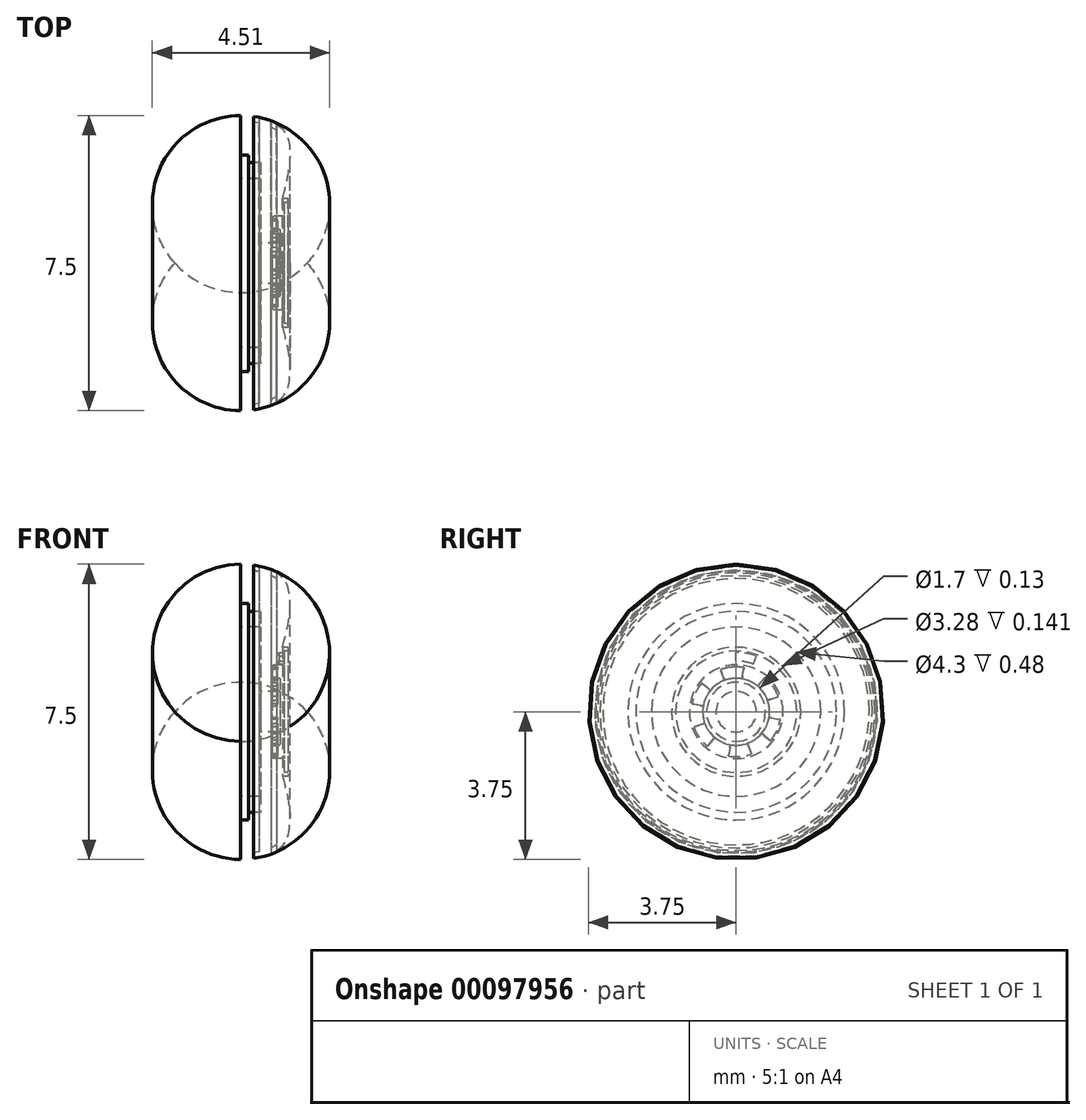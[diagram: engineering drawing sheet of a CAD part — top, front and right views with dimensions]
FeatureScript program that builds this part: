
annotation { "Feature Type Name" : "Feature", "Feature Type Description" : "" }
export const myFeature = defineFeature(function(context is Context, id is Id, definition is map)
    precondition{}
    {
        {
            var Q0;
            Q0=qCreatedBy(makeId("Front.planeOp"),FACE);
            var sketch = newSketch(context, id + "F0", { "sketchPlane" : qUnion([Q0])});
            skLineSegment(sketch, "E0.top", {"start": v(0.87, 0.85) * mm, "end": v(1, 0.85) * mm});
            skLineSegment(sketch, "E0.right", {"start": v(1, 0.51) * mm, "end": v(1, 0.85) * mm});
            skLineSegment(sketch, "E1", {"start": v(0.8, 0.93) * mm, "end": v(0.8, 1.1) * mm});
            skLineSegment(sketch, "E2", {"start": v(0.87, 1.19) * mm, "end": v(1.1, 1.19) * mm});
            skLineSegment(sketch, "E3", {"start": v(1.12, 1.64) * mm, "end": v(1.06, 1.64) * mm});
            skPoint(sketch, "E4.orphan", {"position": v(0, 1.19) * mm});
            skPoint(sketch, "E5.visualSharp", {"position": v(1.1, 1.19) * mm});
            skPoint(sketch, "E6.visualSharp", {"position": v(0.8, 1.19) * mm});
            skArc(sketch, "E6.filletArc", {"start": v(0.87, 1.19) * mm, "mid": v(0.81, 1.17) * mm, "end": v(0.8, 1.1) * mm});
            skArc(sketch, "E7.filletArc", {"start": v(0.8, 0.93) * mm, "mid": v(0.81, 0.87) * mm, "end": v(0.87, 0.85) * mm});
            skPoint(sketch, "E8.visualSharp", {"position": v(1.2, 1.64) * mm});
            skLineSegment(sketch, "E9", {"start": v(-0.76, 3.75) * mm, "end": v(0, 3.75) * mm, "construction": true});
            skLineSegment(sketch, "E10", {"start": v(1.25, 3.8) * mm, "end": v(1.25, 0.98) * mm, "construction": true});
            skLineSegment(sketch, "E11", {"start": v(0, 3.75) * mm, "end": v(1.72, 3.75) * mm, "construction": true});
            skLineSegment(sketch, "E12", {"start": v(1.25, 1.19) * mm, "end": v(1.27, 1.19) * mm});
            skLineSegment(sketch, "E13", {"start": v(1.1, 1.19) * mm, "end": v(1.1, 1.54) * mm});
            skPoint(sketch, "E14.orphan", {"position": v(0, 0.73) * mm});
            skLineSegment(sketch, "E15", {"start": v(0, 0.73) * mm, "end": v(0, 2.15) * mm, "construction": true});
            skLineSegment(sketch, "E16", {"start": v(0.5, 0.52) * mm, "end": v(1, 0.52) * mm});
            skLineSegment(sketch, "E17", {"start": v(0.57, 0) * mm, "end": v(0.57, -0.77) * mm, "construction": true});
            skLineSegment(sketch, "E18", {"start": v(1.1, 4.64) * mm, "end": v(1.1, 3.06) * mm, "construction": true});
            skLineSegment(sketch, "E19", {"start": v(0.97, 3.34) * mm, "end": v(1.1, 3.34) * mm, "construction": true});
            skFitSpline(sketch, "E20", {"points": [v(1.06, 1.64) * mm, v(1.25, 2.8) * mm, v(1.1, 3.34) * mm, v(0, 3.75) * mm], "startDerivative": vector(1.54, 5.67) * mm, "endDerivative": vector(-4.24, 0) * mm});
            skPoint(sketch, "E21", {"position": v(1.25, 2.38) * mm});
            skLineSegment(sketch, "E22", {"start": v(0.32, 3.93) * mm, "end": v(0.32, 3.59) * mm, "construction": true});
            skLineSegment(sketch, "E23", {"start": v(0.46, 3.93) * mm, "end": v(0.46, 3.56) * mm, "construction": true});
            skLineSegment(sketch, "E24", {"start": v(0.77, 3.93) * mm, "end": v(0.77, 3.46) * mm, "construction": true});
            skLineSegment(sketch, "E25", {"start": v(0.91, 3.95) * mm, "end": v(0.91, 3.38) * mm, "construction": true});
            skLineSegment(sketch, "E26", {"start": v(0.32, 3.59) * mm, "end": v(0.46, 3.56) * mm});
            skLineSegment(sketch, "E27", {"start": v(0.77, 3.46) * mm, "end": v(0.91, 3.38) * mm});
            skLineSegment(sketch, "E28", {"start": v(0.32, 3.73) * mm, "end": v(0.32, 3.59) * mm});
            skLineSegment(sketch, "E29", {"start": v(0.46, 3.56) * mm, "end": v(0.46, 3.7) * mm});
            skLineSegment(sketch, "E30", {"start": v(0.77, 3.46) * mm, "end": v(0.77, 3.6) * mm});
            skLineSegment(sketch, "E31", {"start": v(0.91, 3.38) * mm, "end": v(0.91, 3.52) * mm});
            skLineSegment(sketch, "E32", {"start": v(0, 0.52) * mm, "end": v(0, 2.15) * mm});
            skLineSegment(sketch, "E33", {"start": v(0.02, 0) * mm, "end": v(2.08, 0) * mm, "construction": true});
            skLineSegment(sketch, "E34", {"start": v(0, 0.51) * mm, "end": v(0, 2.15) * mm, "construction": true});
            skLineSegment(sketch, "E35", {"start": v(0, 0.52) * mm, "end": v(0, 0) * mm});
            skLineSegment(sketch, "E36", {"start": v(0, 0) * mm, "end": v(0.5, 0) * mm});
            skLineSegment(sketch, "E37", {"start": v(0.5, 0) * mm, "end": v(0.5, 0.52) * mm});
            skLineSegment(sketch, "E38", {"start": v(1.2, 1.54) * mm, "end": v(1.1, 1.54) * mm});
            skLineSegment(sketch, "E39", {"start": v(1.2, 1.64) * mm, "end": v(1.12, 1.64) * mm});
            skLineSegment(sketch, "E40", {"start": v(1.2, 1.64) * mm, "end": v(1.2, 1.54) * mm});
            skLineSegment(sketch, "E41", {"start": v(0, 2.75) * mm, "end": v(0.2, 2.75) * mm});
            skLineSegment(sketch, "E42", {"start": v(0.2, 2.75) * mm, "end": v(0.2, 2.55) * mm});
            skLineSegment(sketch, "E43", {"start": v(0.2, 2.55) * mm, "end": v(0.5, 2.55) * mm});
            skLineSegment(sketch, "E44", {"start": v(0.5, 2.55) * mm, "end": v(0.5, 2.15) * mm});
            skLineSegment(sketch, "E45", {"start": v(0.5, 2.15) * mm, "end": v(0.02, 2.15) * mm});
            skLineSegment(sketch, "E46.trimOffspring", {"start": v(0, 2.75) * mm, "end": v(0, 5.56) * mm, "construction": true});
            skLineSegment(sketch, "E47.trimOffspring", {"start": v(0, 2.75) * mm, "end": v(0, 5.2) * mm, "construction": true});
            skLineSegment(sketch, "E48.trimOffspring", {"start": v(0, 2.75) * mm, "end": v(0, 3.75) * mm});
            skLineSegment(sketch, "E49", {"start": v(0.02, 0) * mm, "end": v(0.02, 2.15) * mm});
            skSolve(sketch);
        }
        {
            var Q0;
            Q0=makeQuery(id+"F0.imprint","IMPRINT",FACE,{"disambiguationData":[TD([[makeQuery(id+"F0.imprint","IMPRINT",EDGE,{"derivedFrom":sQuery(id+"F0.wireOp",EDGE,"E0.top")}),-1.0]])]});
            var Q1;
            Q1=sQuery(id+"F0.wireOp",EDGE,"8bb111fc-4642-4fca-a44e-8b574824e9490.MirrorCS");
            var Q2;
            Q2=sQuery(id+"F0.wireOp",EDGE,"5d76dffb-9663-4801-85ba-127905f750e50.MirrorCS");
            var Q3;
            Q3=sQuery(id+"F0.wireOp",EDGE,"d13460d5-a523-4224-9297-77c6a2cba0c50.MirrorCS");
            var Q4;
            Q4=sQuery(id+"F0.wireOp",EDGE,"c0737af9-8dda-4185-ab45-cae04200aa6d0.MirrorCS");
            var Q5;
            Q5=sQuery(id+"F0.wireOp",EDGE,"E33");
            revolve(context, id + "F1", {"entities" : qUnion([Q0]), "surfaceEntities" : qUnion([Q1, Q2, Q3, Q4]), "axis" : qUnion([Q5]), "revolveType" : RevolveType.FULL});
        }
        {
            var Q0;
            Q0=qCreatedBy(makeId("Front.planeOp"),FACE);
            var sketch = newSketch(context, id + "F2", { "sketchPlane" : qUnion([Q0])});
            skLineSegment(sketch, "E50.bottom", {"start": v(0.97, 1.51) * mm, "end": v(1.17, 1.51) * mm});
            skLineSegment(sketch, "E50.top", {"start": v(0.97, 1.29) * mm, "end": v(1.17, 1.29) * mm});
            skLineSegment(sketch, "E50.left", {"start": v(0.97, 1.51) * mm, "end": v(0.97, 1.29) * mm});
            skLineSegment(sketch, "E50.right", {"start": v(1.17, 1.51) * mm, "end": v(1.17, 1.29) * mm});
            skLineSegment(sketch, "E51", {"start": v(0, 0) * mm, "end": v(2.72, 0) * mm, "construction": true});
            skSolve(sketch);
        }
        {
            var Q0;
            Q0=qSketchRegion(id+"F2",true);
            var Q1;
            Q1=sQuery(id+"F2.wireOp",EDGE,"E51");
            revolve(context, id + "F3", {"operationType" : NewBodyOperationType.REMOVE, "entities" : qUnion([Q0]), "axis" : qUnion([Q1]), "revolveType" : RevolveType.ONE_DIRECTION, "oppositeDirection" : true, "angle" : 20 * degree});
        }
        {
            var Q0;
            Q0=makeQuery(id+"F1.opRevolve","SWEPT_FACE",FACE,{"disambiguationData":[OSD([sQuery(id+"F0.wireOp",EDGE,"E1")])]});
            var sketch = newSketch(context, id + "F4", { "sketchPlane" : qUnion([Q0])});
            skLineSegment(sketch, "E52", {"start": v(-0.27, 0.74) * mm, "end": v(-0.39, 1.07) * mm});
            skArc(sketch, "E53", {"start": v(-0.39, 1.07) * mm, "mid": v(-0.1, 1.13) * mm, "end": v(0.2, 1.12) * mm});
            skLineSegment(sketch, "E54", {"start": v(0.14, 0.78) * mm, "end": v(0.2, 1.12) * mm});
            skArc(sketch, "E55", {"start": v(-0.27, 0.74) * mm, "mid": v(-0.07, 0.79) * mm, "end": v(0.14, 0.78) * mm});
            skLineSegment(sketch, "E56.1.0", {"start": v(-0.78, 0.14) * mm, "end": v(-1.12, 0.2) * mm});
            skArc(sketch, "E56.1.1", {"start": v(-1.12, 0.2) * mm, "mid": v(-1.03, 0.48) * mm, "end": v(-0.87, 0.73) * mm});
            skLineSegment(sketch, "E56.1.2", {"start": v(-0.6, 0.5) * mm, "end": v(-0.87, 0.73) * mm});
            skArc(sketch, "E56.1.3", {"start": v(-0.78, 0.14) * mm, "mid": v(-0.71, 0.33) * mm, "end": v(-0.6, 0.5) * mm});
            skLineSegment(sketch, "E56.2.0", {"start": v(-0.5, -0.6) * mm, "end": v(-0.73, -0.87) * mm});
            skArc(sketch, "E56.2.1", {"start": v(-0.73, -0.87) * mm, "mid": v(-0.93, -0.65) * mm, "end": v(-1.07, -0.39) * mm});
            skLineSegment(sketch, "E56.2.2", {"start": v(-0.74, -0.27) * mm, "end": v(-1.07, -0.39) * mm});
            skArc(sketch, "E56.2.3", {"start": v(-0.5, -0.6) * mm, "mid": v(-0.65, -0.45) * mm, "end": v(-0.74, -0.27) * mm});
            skLineSegment(sketch, "E57.1.3.0", {"start": v(0.27, -0.74) * mm, "end": v(0.39, -1.07) * mm});
            skArc(sketch, "E57.3.3.0", {"start": v(0.39, -1.07) * mm, "mid": v(0.1, -1.13) * mm, "end": v(-0.2, -1.12) * mm});
            skLineSegment(sketch, "E57.7.3.0", {"start": v(-0.14, -0.78) * mm, "end": v(-0.2, -1.12) * mm});
            skArc(sketch, "E57.10.3.0", {"start": v(0.27, -0.74) * mm, "mid": v(0.07, -0.79) * mm, "end": v(-0.14, -0.78) * mm});
            skLineSegment(sketch, "E57.1.4.0", {"start": v(0.78, -0.14) * mm, "end": v(1.12, -0.2) * mm});
            skArc(sketch, "E57.3.4.0", {"start": v(1.12, -0.2) * mm, "mid": v(1.03, -0.48) * mm, "end": v(0.87, -0.73) * mm});
            skLineSegment(sketch, "E57.7.4.0", {"start": v(0.6, -0.5) * mm, "end": v(0.87, -0.73) * mm});
            skArc(sketch, "E57.10.4.0", {"start": v(0.78, -0.14) * mm, "mid": v(0.71, -0.33) * mm, "end": v(0.6, -0.5) * mm});
            skLineSegment(sketch, "E57.1.5.0", {"start": v(0.5, 0.6) * mm, "end": v(0.73, 0.87) * mm});
            skArc(sketch, "E57.3.5.0", {"start": v(0.73, 0.87) * mm, "mid": v(0.93, 0.65) * mm, "end": v(1.07, 0.39) * mm});
            skLineSegment(sketch, "E57.7.5.0", {"start": v(0.74, 0.27) * mm, "end": v(1.07, 0.39) * mm});
            skArc(sketch, "E57.10.5.0", {"start": v(0.5, 0.6) * mm, "mid": v(0.65, 0.45) * mm, "end": v(0.74, 0.27) * mm});
            skSolve(sketch);
        }
        {
            var Q0;
            Q0=qSketchRegion(id+"F4",true);
            extrude(context, id + "F5", {"entities" : qUnion([Q0]), "operationType" : NewBodyOperationType.ADD, "depth" : .15 * mm});
        }
    });
